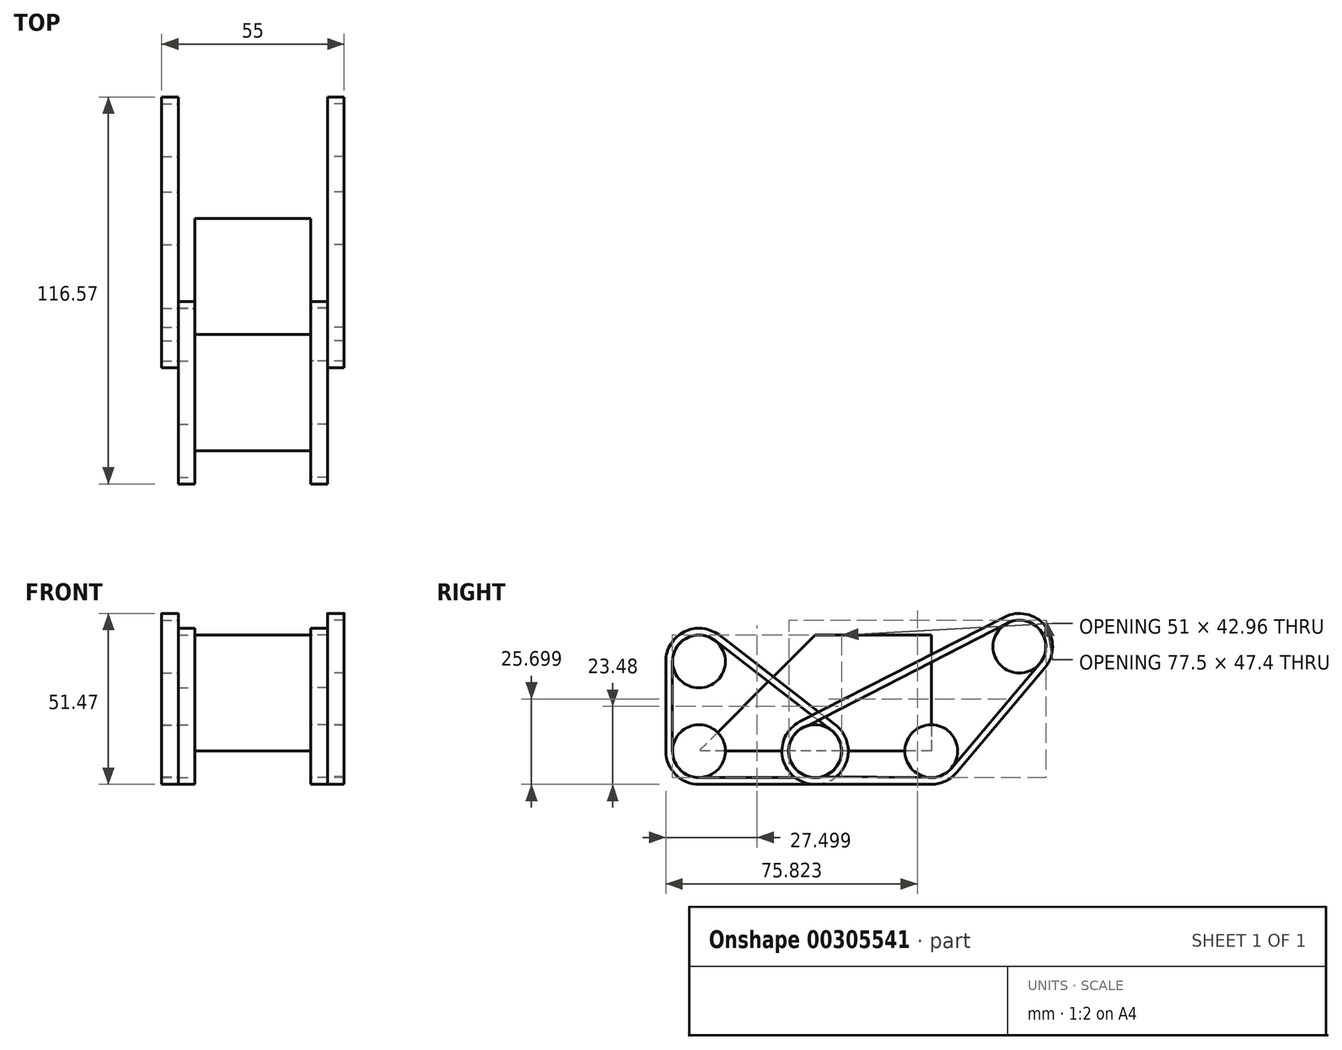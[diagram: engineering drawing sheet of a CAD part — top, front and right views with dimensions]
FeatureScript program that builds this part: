
annotation { "Feature Type Name" : "Feature", "Feature Type Description" : "" }
export const myFeature = defineFeature(function(context is Context, id is Id, definition is map)
    precondition{}
    {
        {
            var Q0;
            Q0=qCreatedBy(makeId("Top.planeOp"),FACE);
            var sketch = newSketch(context, id + "F0", { "sketchPlane" : qUnion([Q0])});
            skLineSegment(sketch, "E0.bottom", {"start": v(-17.5, 35) * mm, "end": v(17.5, 35) * mm});
            skLineSegment(sketch, "E0.top", {"start": v(-17.5, -35) * mm, "end": v(17.5, -35) * mm});
            skLineSegment(sketch, "E0.left", {"start": v(-17.5, 35) * mm, "end": v(-17.5, -35) * mm});
            skLineSegment(sketch, "E0.right", {"start": v(17.5, 35) * mm, "end": v(17.5, -35) * mm});
            skPoint(sketch, "E0.middle", {"position": v(0, 0) * mm});
            skSolve(sketch);
        }
        {
            var Q0;
            Q0 = qSketchRegion(id + "F0", true);
            extrude(context, id + "F1", {"entities" : qUnion([Q0]), "depth" : 35 * mm});
        }
        {
            var Q0;
            Q0=makeQuery(id+"F1.opExtrude","SWEPT_FACE",FACE,{"disambiguationData":[OSD([sQuery(id+"F0.wireOp",EDGE,"E0.right")])]});
            var sketch = newSketch(context, id + "F2", { "sketchPlane" : qUnion([Q0])});
            skLineSegment(sketch, "E1.0", {"start": v(35, 35) * mm, "end": v(-35, 35) * mm});
            skLineSegment(sketch, "E2.0", {"start": v(35, 35) * mm, "end": v(35, 0) * mm});
            skPoint(sketch, "E3.0", {"position": v(-35, 17.5) * mm});
            skLineSegment(sketch, "E4", {"start": v(0, 35) * mm, "end": v(-35, 0) * mm});
            skSolve(sketch);
        }
        {
            var Q0;
            {var subQ2=sQuery(id+"F2.wireOp",EDGE,"E4");Q0=makeQuery(id+"F2.imprint","IMPRINT",FACE,{"disambiguationData":[TD([[makeQuery(id+"F2.imprint","IMPRINT",EDGE,{"derivedFrom":subQ2}),-1.0]])]});}
            extrude(context, id + "F3", {"entities" : qUnion([Q0]), "operationType" : NewBodyOperationType.REMOVE, "endBound" : BoundingType.THROUGH_ALL, "oppositeDirection" : true, "depth" : 25 * mm});
        }
        {
            var Q0;
            Q0=makeQuery(id+"F1.opExtrude","SWEPT_FACE",FACE,{"disambiguationData":[OSD([sQuery(id+"F0.wireOp",EDGE,"E0.right")])]});
            var sketch = newSketch(context, id + "F4", { "sketchPlane" : qUnion([Q0])});
            skCircle(sketch, "E5", {"center": v(0, 0) * mm, "radius": 7.95 * mm});
            skCircle(sketch, "E6", {"center": v(-35, 27) * mm, "radius": 7.95 * mm});
            skCircle(sketch, "E7", {"center": v(-35, 0) * mm, "radius": 7.95 * mm});
            skArc(sketch, "E8", {"start": v(-28.9, 34.92) * mm, "mid": v(-39.41, 35.97) * mm, "end": v(-45, 27) * mm});
            skArc(sketch, "E9", {"start": v(-45, 0) * mm, "mid": v(-42.07, -7.07) * mm, "end": v(-35, -10) * mm});
            skArc(sketch, "E10", {"start": v(0, -10) * mm, "mid": v(9.47, -3.23) * mm, "end": v(6.1, 7.92) * mm});
            skLineSegment(sketch, "E11", {"start": v(-45, 27) * mm, "end": v(-45, 0) * mm});
            skLineSegment(sketch, "E12", {"start": v(-35, -10) * mm, "end": v(0, -10) * mm});
            skLineSegment(sketch, "E13", {"start": v(-28.9, 34.92) * mm, "end": v(6.1, 7.92) * mm});
            skArc(sketch, "E14", {"start": v(-30.11, 33.33) * mm, "mid": v(-38.53, 34.18) * mm, "end": v(-43, 27) * mm});
            skArc(sketch, "E15", {"start": v(-43, 0) * mm, "mid": v(-40.66, -5.66) * mm, "end": v(-35, -8) * mm});
            skArc(sketch, "E16", {"start": v(0, -8) * mm, "mid": v(7.57, -2.58) * mm, "end": v(4.89, 6.33) * mm});
            skLineSegment(sketch, "E17", {"start": v(0, -8) * mm, "end": v(-35, -8) * mm});
            skLineSegment(sketch, "E18", {"start": v(-43, 0) * mm, "end": v(-43, 27) * mm});
            skLineSegment(sketch, "E19", {"start": v(-30.11, 33.33) * mm, "end": v(4.89, 6.33) * mm});
            skCircle(sketch, "E20", {"center": v(-35, 0) * mm, "radius": 2.5 * mm});
            skCircle(sketch, "E21", {"center": v(-35, 27) * mm, "radius": 2.5 * mm});
            skCircle(sketch, "E22", {"center": v(0, 0) * mm, "radius": 2.5 * mm});
            skArc(sketch, "E23.MirrorCS", {"start": v(0, -8) * mm, "mid": v(-7.57, -2.58) * mm, "end": v(-4.89, 6.33) * mm});
            skSolve(sketch);
        }
        {
            var Q0;
            {var subQ0=sQuery(id+"F4.wireOp",EDGE,"UBWbRd6a-DJoe-i8ud-jSSl-dXQvjHMN57V0");var subQ1=sQuery(id+"F4.wireOp",EDGE,"E10");var subQ2=makeQuery(id+"F4.imprint","INTERSECT",VERTEX,{"derivedFrom":[subQ1,subQ0]});Q0=makeQuery(id+"F4.imprint","IMPRINT",FACE,{"disambiguationData":[TD([[makeQuery(id+"F4.imprint","IMPRINT",EDGE,{"disambiguationData":[TD([[subQ2,-1.0]])],"derivedFrom":subQ1}),1.0]])]});}
            var Q1;
            {var subQ0=sQuery(id+"F4.wireOp",EDGE,"jzU2OQ95-UY80-Eo5W-r00L-1yaV5iknPwUe");var subQ1=sQuery(id+"F4.wireOp",EDGE,"E10");var subQ2=makeQuery(id+"F4.imprint","INTERSECT",VERTEX,{"derivedFrom":[subQ1,subQ0]});Q1=makeQuery(id+"F4.imprint","IMPRINT",FACE,{"disambiguationData":[TD([[makeQuery(id+"F4.imprint","IMPRINT",EDGE,{"disambiguationData":[TD([[subQ2,1.0]])],"derivedFrom":subQ1}),1.0]])]});}
            var Q2;
            {var subQ3=sQuery(id+"F4.wireOp",EDGE,"E8");Q2=makeQuery(id+"F4.imprint","IMPRINT",FACE,{"disambiguationData":[TD([[makeQuery(id+"F4.imprint","IMPRINT",EDGE,{"derivedFrom":subQ3}),1.0]])]});}
            var Q3;
            {var subQ5=sQuery(id+"F4.wireOp",EDGE,"E10");var subQ7=sQuery(id+"F4.wireOp",EDGE,"E13");var subQ8=makeQuery(id+"F4.imprint","INTERSECT",VERTEX,{"derivedFrom":[subQ5,subQ7]});Q3=makeQuery(id+"F4.imprint","IMPRINT",FACE,{"disambiguationData":[TD([[makeQuery(id+"F4.imprint","IMPRINT",EDGE,{"disambiguationData":[TD([[subQ8,1.0]])],"derivedFrom":subQ5}),1.0]])]});}
            var Q4;
            {var subQ1=sQuery(id+"F0.wireOp",EDGE,"E0.right");var subQ2=makeQuery(id+"F1.opExtrude","CAP_EDGE",EDGE,{"disambiguationData":[OSD([subQ1])],"isStart":false});var subQ4=sQuery(id+"F4.wireOp",EDGE,"E13");var subQ5=makeQuery(id+"F4.imprint","INTERSECT",VERTEX,{"derivedFrom":[subQ2,subQ4]});Q4=makeQuery(id+"F4.imprint","IMPRINT",FACE,{"disambiguationData":[TD([[makeQuery(id+"F4.imprint","IMPRINT",EDGE,{"disambiguationData":[TD([[subQ5,-1.0]])],"derivedFrom":subQ4}),-1.0]])]});}
            var Q5;
            {var subQ0=sQuery(id+"F4.wireOp",EDGE,"E6");var subQ1=makeQuery(id+"F1.opExtrude","SWEPT_EDGE",EDGE,{"disambiguationData":[OSD([sQuery(id+"F0.wireOp",EDGE,"E0.top"),sQuery(id+"F0.wireOp",EDGE,"E0.right")])]});var subQ2=makeQuery(id+"F4.imprint","INTERSECT",VERTEX,{"disambiguationData":[OD(0.0)],"derivedFrom":[subQ1,subQ0]});Q5=makeQuery(id+"F4.imprint","IMPRINT",FACE,{"disambiguationData":[TD([[makeQuery(id+"F4.imprint","IMPRINT",EDGE,{"disambiguationData":[TD([[subQ2,1.0]])],"derivedFrom":subQ0}),1.0]])]});}
            var Q6;
            {var subQ0=sQuery(id+"F4.wireOp",EDGE,"E6");var subQ1=makeQuery(id+"F1.opExtrude","SWEPT_EDGE",EDGE,{"disambiguationData":[OSD([sQuery(id+"F0.wireOp",EDGE,"E0.top"),sQuery(id+"F0.wireOp",EDGE,"E0.right")])]});var subQ2=makeQuery(id+"F4.imprint","INTERSECT",VERTEX,{"disambiguationData":[OD(0.0)],"derivedFrom":[subQ1,subQ0]});Q6=makeQuery(id+"F4.imprint","IMPRINT",FACE,{"disambiguationData":[TD([[makeQuery(id+"F4.imprint","IMPRINT",EDGE,{"disambiguationData":[TD([[subQ2,-1.0]])],"derivedFrom":subQ0}),1.0]])]});}
            var Q7;
            {var subQ1=sQuery(id+"F0.wireOp",EDGE,"E0.right");var subQ4=makeQuery(id+"F1.opExtrude","CAP_EDGE",EDGE,{"disambiguationData":[OSD([subQ1])],"isStart":true});var subQ6=sQuery(id+"F4.wireOp",EDGE,"E20");var subQ7=makeQuery(id+"F4.imprint","INTERSECT",VERTEX,{"derivedFrom":[subQ4,subQ6]});Q7=makeQuery(id+"F4.imprint","IMPRINT",FACE,{"disambiguationData":[TD([[makeQuery(id+"F4.imprint","IMPRINT",EDGE,{"disambiguationData":[TD([[subQ7,1.0]])],"derivedFrom":subQ4}),1.0]])]});}
            var Q8;
            {var subQ1=sQuery(id+"F0.wireOp",EDGE,"E0.right");var subQ4=makeQuery(id+"F1.opExtrude","CAP_EDGE",EDGE,{"disambiguationData":[OSD([subQ1])],"isStart":true});var subQ6=sQuery(id+"F4.wireOp",EDGE,"E20");var subQ8=makeQuery(id+"F4.imprint","INTERSECT",VERTEX,{"derivedFrom":[subQ4,subQ6]});Q8=makeQuery(id+"F4.imprint","IMPRINT",FACE,{"disambiguationData":[TD([[makeQuery(id+"F4.imprint","IMPRINT",EDGE,{"disambiguationData":[TD([[subQ8,1.0]])],"derivedFrom":subQ4}),-1.0]])]});}
            var Q9;
            {var subQ0=sQuery(id+"F4.wireOp",EDGE,"E5");var subQ1=makeQuery(id+"F1.opExtrude","CAP_EDGE",EDGE,{"disambiguationData":[OSD([sQuery(id+"F0.wireOp",EDGE,"E0.right")])],"isStart":true});var subQ2=makeQuery(id+"F4.imprint","INTERSECT",VERTEX,{"derivedFrom":[subQ1,subQ0]});Q9=makeQuery(id+"F4.imprint","IMPRINT",FACE,{"disambiguationData":[TD([[makeQuery(id+"F4.imprint","IMPRINT",EDGE,{"disambiguationData":[TD([[subQ2,1.0]])],"derivedFrom":subQ0}),1.0]])]});}
            var Q10;
            {var subQ0=sQuery(id+"F4.wireOp",EDGE,"E21");var subQ1=makeQuery(id+"F1.opExtrude","SWEPT_EDGE",EDGE,{"disambiguationData":[OSD([sQuery(id+"F0.wireOp",EDGE,"E0.top"),sQuery(id+"F0.wireOp",EDGE,"E0.right")])]});var subQ2=makeQuery(id+"F4.imprint","INTERSECT",VERTEX,{"disambiguationData":[OD(0.0)],"derivedFrom":[subQ1,subQ0]});Q10=makeQuery(id+"F4.imprint","IMPRINT",FACE,{"disambiguationData":[TD([[makeQuery(id+"F4.imprint","IMPRINT",EDGE,{"disambiguationData":[TD([[subQ2,1.0]])],"derivedFrom":subQ0}),1.0]])]});}
            var Q11;
            {var subQ0=sQuery(id+"F4.wireOp",EDGE,"E21");var subQ1=makeQuery(id+"F1.opExtrude","SWEPT_EDGE",EDGE,{"disambiguationData":[OSD([sQuery(id+"F0.wireOp",EDGE,"E0.top"),sQuery(id+"F0.wireOp",EDGE,"E0.right")])]});var subQ2=makeQuery(id+"F4.imprint","INTERSECT",VERTEX,{"disambiguationData":[OD(0.0)],"derivedFrom":[subQ1,subQ0]});Q11=makeQuery(id+"F4.imprint","IMPRINT",FACE,{"disambiguationData":[TD([[makeQuery(id+"F4.imprint","IMPRINT",EDGE,{"disambiguationData":[TD([[subQ2,-1.0]])],"derivedFrom":subQ0}),1.0]])]});}
            var Q12;
            {var subQ0=sQuery(id+"F4.wireOp",EDGE,"E20");var subQ1=sQuery(id+"F0.wireOp",EDGE,"E0.right");var subQ4=makeQuery(id+"F1.opExtrude","CAP_EDGE",EDGE,{"disambiguationData":[OSD([subQ1])],"isStart":true});var subQ5=makeQuery(id+"F4.imprint","INTERSECT",VERTEX,{"derivedFrom":[subQ4,subQ0]});Q12=makeQuery(id+"F4.imprint","IMPRINT",FACE,{"disambiguationData":[TD([[makeQuery(id+"F4.imprint","IMPRINT",EDGE,{"disambiguationData":[TD([[subQ5,-1.0]])],"derivedFrom":subQ0}),1.0]])]});}
            var Q13;
            {var subQ0=sQuery(id+"F4.wireOp",EDGE,"E20");var subQ1=sQuery(id+"F0.wireOp",EDGE,"E0.right");var subQ4=makeQuery(id+"F1.opExtrude","CAP_EDGE",EDGE,{"disambiguationData":[OSD([subQ1])],"isStart":true});var subQ5=makeQuery(id+"F4.imprint","INTERSECT",VERTEX,{"derivedFrom":[subQ4,subQ0]});Q13=makeQuery(id+"F4.imprint","IMPRINT",FACE,{"disambiguationData":[TD([[makeQuery(id+"F4.imprint","IMPRINT",EDGE,{"disambiguationData":[TD([[subQ5,1.0]])],"derivedFrom":subQ0}),1.0]])]});}
            var Q14;
            {var subQ0=sQuery(id+"F4.wireOp",EDGE,"E22");var subQ1=makeQuery(id+"F1.opExtrude","CAP_EDGE",EDGE,{"disambiguationData":[OSD([sQuery(id+"F0.wireOp",EDGE,"E0.right")])],"isStart":true});var subQ2=makeQuery(id+"F4.imprint","INTERSECT",VERTEX,{"derivedFrom":[subQ1,subQ0]});Q14=makeQuery(id+"F4.imprint","IMPRINT",FACE,{"disambiguationData":[TD([[makeQuery(id+"F4.imprint","IMPRINT",EDGE,{"disambiguationData":[TD([[subQ2,1.0]])],"derivedFrom":subQ0}),1.0]])]});}
            var Q15;
            {var subQ0=sQuery(id+"F4.wireOp",EDGE,"E5");var subQ1=makeQuery(id+"F1.opExtrude","CAP_EDGE",EDGE,{"disambiguationData":[OSD([sQuery(id+"F0.wireOp",EDGE,"E0.right")])],"isStart":true});var subQ2=makeQuery(id+"F4.imprint","INTERSECT",VERTEX,{"derivedFrom":[subQ1,subQ0]});Q15=makeQuery(id+"F4.imprint","IMPRINT",FACE,{"disambiguationData":[TD([[makeQuery(id+"F4.imprint","IMPRINT",EDGE,{"disambiguationData":[TD([[subQ2,-1.0]])],"derivedFrom":subQ0}),1.0]])]});}
            var Q16;
            {var subQ5=sQuery(id+"F4.wireOp",EDGE,"E16");Q16=makeQuery(id+"F4.imprint","IMPRINT",FACE,{"disambiguationData":[TD([[makeQuery(id+"F4.imprint","IMPRINT",EDGE,{"derivedFrom":subQ5}),-1.0]])]});}
            var Q17;
            {var subQ0=sQuery(id+"F4.wireOp",EDGE,"smODPsph-A6uk-QWGb-EGSb-wxFAXmoXFzKu");var subQ1=sQuery(id+"F4.wireOp",EDGE,"E5");var subQ2=makeQuery(id+"F4.imprint","INTERSECT",VERTEX,{"derivedFrom":[subQ1,subQ0]});Q17=makeQuery(id+"F4.imprint","IMPRINT",FACE,{"disambiguationData":[TD([[makeQuery(id+"F4.imprint","IMPRINT",EDGE,{"disambiguationData":[TD([[subQ2,-1.0]])],"derivedFrom":subQ1}),1.0]])]});}
            var Q18;
            {var subQ0=sQuery(id+"F4.wireOp",EDGE,"smODPsph-A6uk-QWGb-EGSb-wxFAXmoXFzKu");var subQ1=sQuery(id+"F4.wireOp",EDGE,"E5");var subQ2=makeQuery(id+"F4.imprint","INTERSECT",VERTEX,{"derivedFrom":[subQ1,subQ0]});Q18=makeQuery(id+"F4.imprint","IMPRINT",FACE,{"disambiguationData":[TD([[makeQuery(id+"F4.imprint","IMPRINT",EDGE,{"disambiguationData":[TD([[subQ2,1.0]])],"derivedFrom":subQ1}),1.0]])]});}
            var Q19;
            {var subQ0=sQuery(id+"F4.wireOp",EDGE,"smODPsph-A6uk-QWGb-EGSb-wxFAXmoXFzKu");var subQ1=sQuery(id+"F4.wireOp",EDGE,"E22");var subQ2=makeQuery(id+"F4.imprint","INTERSECT",VERTEX,{"derivedFrom":[subQ1,subQ0]});Q19=makeQuery(id+"F4.imprint","IMPRINT",FACE,{"disambiguationData":[TD([[makeQuery(id+"F4.imprint","IMPRINT",EDGE,{"disambiguationData":[TD([[subQ2,-1.0]])],"derivedFrom":subQ1}),1.0]])]});}
            var Q20;
            {var subQ0=sQuery(id+"F4.wireOp",EDGE,"BwTRTwZt-QGp7-30l6-qukD-OCgXNmfHvWPs");var subQ1=sQuery(id+"F4.wireOp",EDGE,"E22");var subQ2=makeQuery(id+"F4.imprint","INTERSECT",VERTEX,{"derivedFrom":[subQ1,subQ0]});Q20=makeQuery(id+"F4.imprint","IMPRINT",FACE,{"disambiguationData":[TD([[makeQuery(id+"F4.imprint","IMPRINT",EDGE,{"disambiguationData":[TD([[subQ2,1.0]])],"derivedFrom":subQ1}),1.0]])]});}
            var Q21;
            {var subQ0=sQuery(id+"F4.wireOp",EDGE,"smODPsph-A6uk-QWGb-EGSb-wxFAXmoXFzKu");var subQ1=sQuery(id+"F4.wireOp",EDGE,"E22");var subQ2=makeQuery(id+"F4.imprint","INTERSECT",VERTEX,{"derivedFrom":[subQ1,subQ0]});Q21=makeQuery(id+"F4.imprint","IMPRINT",FACE,{"disambiguationData":[TD([[makeQuery(id+"F4.imprint","IMPRINT",EDGE,{"disambiguationData":[TD([[subQ2,1.0]])],"derivedFrom":subQ1}),1.0]])]});}
            var Q22;
            Q22=makeQuery(id+"F4.imprint","IMPRINT",FACE,{"disambiguationData":[TD([[makeQuery(id+"F4.imprint","IMPRINT",EDGE,{"derivedFrom":sQuery(id+"F4.wireOp",EDGE,"E6")}),1.0]])]});
            extrude(context, id + "F5", {"entities" : qUnion([Q0, Q1, Q2, Q3, Q4, Q5, Q6, Q7, Q8, Q9, Q10, Q11, Q12, Q13, Q14, Q15, Q16, Q17, Q18, Q19, Q20, Q21, Q22]), "operationType" : NewBodyOperationType.ADD, "depth" : 5 * mm});
        }
        {
            var Q0;
            Q0 = qSketchRegion(id + "F4", true);
            var Q1;
            {var subQ0=sQuery(id+"F4.wireOp",EDGE,"GjctuuD9-Hk4c-nokn-HUmH-snnVZb0mlzF2");var subQ1=makeQuery(id+"F4.imprint","INTERSECT",VERTEX,{"derivedFrom":[sQuery(id+"F4.wireOp",EDGE,"1on1H2tf-1kNL-YQqA-943j-MmMFLcLnEEx1"),subQ0]});Q1=makeQuery(id+"F4.imprint","IMPRINT",FACE,{"disambiguationData":[TD([[makeQuery(id+"F4.imprint","IMPRINT",EDGE,{"disambiguationData":[TD([[subQ1,-1.0]])],"derivedFrom":subQ0}),1.0]])]});}
            var Q2;
            {var subQ0=sQuery(id+"F4.wireOp",EDGE,"pCSujTds-T1vm-3gSX-GYVe-zBWlBLdNwFgE");var subQ1=makeQuery(id+"F4.imprint","INTERSECT",VERTEX,{"derivedFrom":[sQuery(id+"F4.wireOp",EDGE,"UU0pyUC4-TTrF-aTy7-00N9-0K6UFaBb9SMI"),subQ0]});Q2=makeQuery(id+"F4.imprint","IMPRINT",FACE,{"disambiguationData":[TD([[makeQuery(id+"F4.imprint","IMPRINT",EDGE,{"disambiguationData":[TD([[subQ1,1.0]])],"derivedFrom":subQ0}),1.0]])]});}
            extrude(context, id + "F6", {"entities" : qUnion([Q0, Q1, Q2]), "operationType" : NewBodyOperationType.ADD, "depth" : 5 * mm});
        }
        {
            var Q0;
            Q0=makeQuery(id+"F1.opExtrude","SWEPT_BODY",BODY,{"disambiguationData":[OSD([sQuery(id+"F0.wireOp",EDGE,"E0.bottom"),sQuery(id+"F0.wireOp",EDGE,"E0.top"),sQuery(id+"F0.wireOp",EDGE,"E0.left"),sQuery(id+"F0.wireOp",EDGE,"E0.right")])]});
            var Q1;
            Q1=makeQuery(id+"F5.opExtrude","SWEPT_BODY",BODY,{"disambiguationData":[OSD([sQuery(id+"F4.wireOp",EDGE,"E6"),sQuery(id+"F4.wireOp",EDGE,"E21")])]});
            var Q2;
            Q2=qCreatedBy(makeId("Right.planeOp"),FACE);
            mirror(context, id + "F7", {"operationType" : NewBodyOperationType.ADD, "entities" : qUnion([Q0, Q1]), "mirrorPlane" : qUnion([Q2])});
        }
        {
            var Q0;
            Q0=makeQuery(id+"F5.opExtrude","CAP_FACE",FACE,{"disambiguationData":[OSD([sQuery(id+"F4.wireOp",EDGE,"E5")])],"isStart":false});
            var sketch = newSketch(context, id + "F8", { "sketchPlane" : qUnion([Q0])});
            skArc(sketch, "E24", {"start": v(-4.55, 8.9) * mm, "mid": v(-9.72, -2.34) * mm, "end": v(0, -10) * mm});
            skArc(sketch, "E25", {"start": v(35, -10) * mm, "mid": v(39.21, -9.07) * mm, "end": v(42.64, -6.45) * mm});
            skLineSegment(sketch, "E26", {"start": v(0, -10) * mm, "end": v(35, -10) * mm});
            skArc(sketch, "E27", {"start": v(69.21, 25.02) * mm, "mid": v(69.4, 37.69) * mm, "end": v(57.02, 40.37) * mm});
            skLineSegment(sketch, "E28", {"start": v(42.64, -6.45) * mm, "end": v(69.21, 25.02) * mm});
            skLineSegment(sketch, "E29", {"start": v(57.02, 40.37) * mm, "end": v(-4.55, 8.9) * mm});
            skArc(sketch, "E30", {"start": v(67.68, 26.3) * mm, "mid": v(67.83, 36.45) * mm, "end": v(57.9, 38.58) * mm});
            skArc(sketch, "E31", {"start": v(34.92, -8) * mm, "mid": v(38.33, -7.27) * mm, "end": v(41.11, -5.16) * mm});
            skArc(sketch, "E32", {"start": v(-1.89, 7.77) * mm, "mid": v(-7.73, -2.07) * mm, "end": v(2.26, -7.67) * mm});
            skLineSegment(sketch, "E33", {"start": v(2.09, -7.67) * mm, "end": v(34.92, -8) * mm});
            skLineSegment(sketch, "E34", {"start": v(41.11, -5.16) * mm, "end": v(67.68, 26.3) * mm});
            skLineSegment(sketch, "E35", {"start": v(-2.09, 7.67) * mm, "end": v(57.9, 38.58) * mm});
            skCircle(sketch, "E36", {"center": v(0, 0) * mm, "radius": 7.95 * mm});
            skCircle(sketch, "E37", {"center": v(35, 0) * mm, "radius": 7.95 * mm});
            skCircle(sketch, "E38", {"center": v(61.57, 31.47) * mm, "radius": 7.95 * mm});
            skSolve(sketch);
        }
        {
            var Q0;
            Q0 = qSketchRegion(id + "F8", true);
            var Q1;
            Q1=makeQuery(id+"F8.imprint","IMPRINT",FACE,{"disambiguationData":[TD([[makeQuery(id+"F8.imprint","IMPRINT",EDGE,{"derivedFrom":sQuery(id+"F8.wireOp",EDGE,"E37")}),1.0]])]});
            var Q2;
            Q2=makeQuery(id+"F8.imprint","IMPRINT",FACE,{"disambiguationData":[TD([[makeQuery(id+"F8.imprint","IMPRINT",EDGE,{"derivedFrom":sQuery(id+"F8.wireOp",EDGE,"E38")}),1.0]])]});
            var Q3;
            {var subQ0=sQuery(id+"F8.wireOp",EDGE,"E36");var subQ1=makeQuery(id+"F8.imprint","INTERSECT",VERTEX,{"derivedFrom":[sQuery(id+"F8.wireOp",EDGE,"E33"),subQ0]});Q3=makeQuery(id+"F8.imprint","IMPRINT",FACE,{"disambiguationData":[TD([[makeQuery(id+"F8.imprint","IMPRINT",EDGE,{"disambiguationData":[TD([[subQ1,1.0]])],"derivedFrom":subQ0}),1.0]])]});}
            extrude(context, id + "F9", {"entities" : qUnion([Q0, Q1, Q2, Q3]), "operationType" : NewBodyOperationType.ADD, "depth" : 5 * mm});
        }
        {
            var Q0;
            Q0=makeQuery(id+"F1.opExtrude","SWEPT_BODY",BODY,{"disambiguationData":[OSD([sQuery(id+"F0.wireOp",EDGE,"E0.bottom"),sQuery(id+"F0.wireOp",EDGE,"E0.top"),sQuery(id+"F0.wireOp",EDGE,"E0.left"),sQuery(id+"F0.wireOp",EDGE,"E0.right")])]});
            var Q1;
            Q1=makeQuery(id+"F9.opExtrude","SWEPT_BODY",BODY,{"disambiguationData":[OSD([sQuery(id+"F8.wireOp",EDGE,"E37")])]});
            var Q2;
            Q2=makeQuery(id+"F9.opExtrude","SWEPT_BODY",BODY,{"disambiguationData":[OSD([sQuery(id+"F8.wireOp",EDGE,"E38")])]});
            var Q3;
            Q3=qCreatedBy(makeId("Right.planeOp"),FACE);
            mirror(context, id + "F10", {"operationType" : NewBodyOperationType.ADD, "entities" : qUnion([Q0, Q1, Q2]), "mirrorPlane" : qUnion([Q3])});
        }
    });
